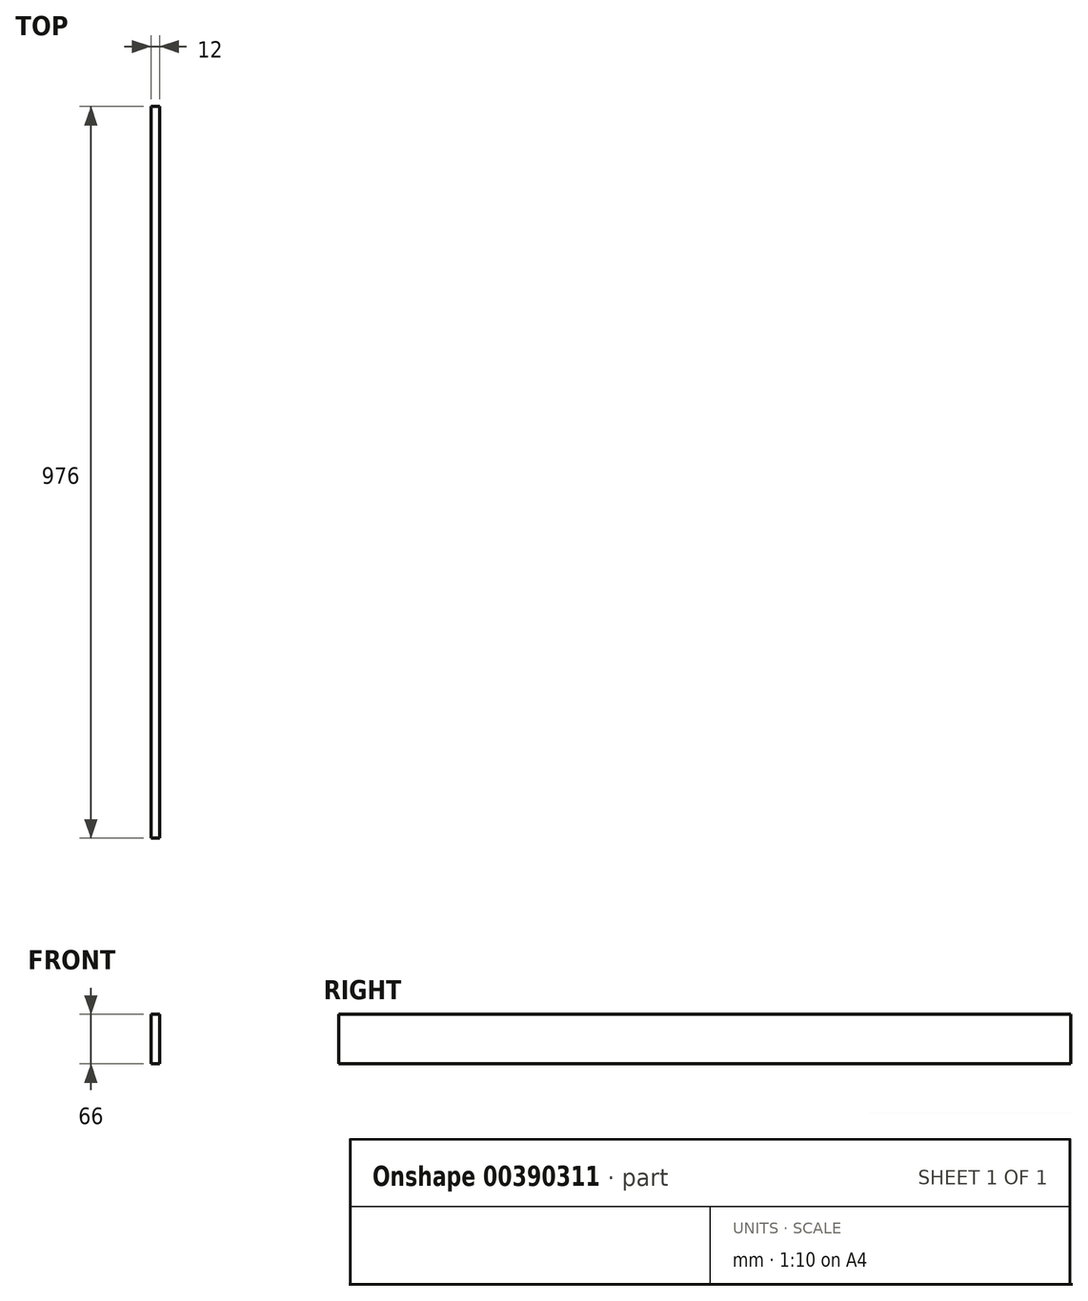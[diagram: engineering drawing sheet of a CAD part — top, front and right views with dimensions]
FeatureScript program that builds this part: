
annotation { "Feature Type Name" : "Feature", "Feature Type Description" : "" }
export const myFeature = defineFeature(function(context is Context, id is Id, definition is map)
    precondition{}
    {
        {
            var Q0;
            Q0=qCreatedBy(makeId("Right.planeOp"),FACE);
            var sketch = newSketch(context, id + "F0", { "sketchPlane" : qUnion([Q0])});
            skLineSegment(sketch, "E0.bottom", {"start": v(0, 0) * mm, "end": v(976, 0) * mm});
            skLineSegment(sketch, "E0.top", {"start": v(0, 66) * mm, "end": v(976, 66) * mm});
            skLineSegment(sketch, "E0.left", {"start": v(0, 0) * mm, "end": v(0, 66) * mm});
            skLineSegment(sketch, "E0.right", {"start": v(976, 0) * mm, "end": v(976, 66) * mm});
            skSolve(sketch);
        }
        {
            var Q0;
            Q0=makeQuery(id+"F0.imprint","IMPRINT",FACE,{"disambiguationData":[TD([[makeQuery(id+"F0.imprint","IMPRINT",EDGE,{"derivedFrom":sQuery(id+"F0.wireOp",EDGE,"E0.bottom")}),1.0]])]});
            extrude(context, id + "F1", {"entities" : qUnion([Q0]), "depth" : 12 * mm});
        }
    });
